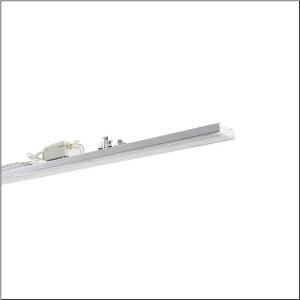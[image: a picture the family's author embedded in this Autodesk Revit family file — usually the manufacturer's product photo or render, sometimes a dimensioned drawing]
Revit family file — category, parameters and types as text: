
# Revit family: licross_11_recessed_mo_51tl18cn49xg
name_source: partatom
category: Lighting Fixtures
units: mm (PartAtom-declared; Revit-internal decimal feet)

## family parameters
Cut with Voids When Loaded = No
Host = Face
Light Source = No
Part Type = Normal
Room Calculation Point = No
Round Connector Dimension = Use Diameter
Shared = No

## types (1)
- --- (1 x LED, 9040 lm, 49.3 W, 4000K)
    Apparent Load = 49 VA
    CIE Flux Codes = 83 96 99 100 100
    Color Rendering = 80
    Color Temperature = 4000K
    Default Elevation = 1800 mm
    Description = Licross 11 Recessed MO, luminaire insert, of sheet steel, coil coated, white, length: 1.500mm, width: 66mm, height: 67mm, LED rated luminous flux: 9.040lm, light colour: 840, SDCM (Standard Deviation of Colour Matching)MacAdam ≤ 2 SDCM (initial), control gear: ON/OFF Multilumen, CLOi, with plug, 3-pole, with phase selection, mains connection: 220..240V, AC, 50/60Hz, start of lifetime: 49W, end of service life: 55W, internal wiring halogen-free, primary light control with lens, of plastic, primary optical cover: cover, of PMMA, light emission: direct distribution, primary light characteristic: symmetric, protection rating (complete): IP40, insulation class (complete): insulation class I (protective earthing), certification: CE, ENEC, VDE, UKCA, protection symbol: D if used in an environment without relevant dust loads with corresponding accessories, impact resistance: IK06, permissible ambient temperature for indoor applications: -35..+40°C, corresponds to IFS (International Featured Standards) requirements for safety and quality in the food industry, reducing of maximum allowable ambient temperature of 5°C with ceiling mounting, LABS conformity tested according to VDMA 24364:2018-05, The light source and the operating device comply with the requirements of the Ecodesign Regulation (EU) 2019/2020 and are replaceable in accordance with this regulation, packaging unit: 1 piece
    Height = 58 mm
    Lamp = 1 x LED
    Lamp Light Flux = 9040 lm
    Lamp Power = 49.3 W
    Lamp count = 1
    Length = 1500 mm
    Luminous efficacy = 183 lm/W
    Manufacturer = Siteco
    ModVariant = No
    Model = 51TL18CN49XG
    Mounting Place = Ceiling
    Mounting Type = Pendant
    Number of Poles = 1
    OnlyDefault = Yes
    Power Factor = 1
    Product Name = Licross 11 Recessed MO
    Product group = luminaire insert | ceiling pendant
    ProductGroupID = 901
    Protection Class = Protection class I
    Protection Degree = IP 40
    RLX_Detail_Level = 1
    RLX_Emergency_Light_Flux = 0 lm
    RLX_Emergency_Type = 0
    RLX_Emergency_Type_DB = No
    RlxData = <blob elided: 22577 chars, md5=b130c7b6>
    Socket = socket
    Standby Power = 0 W
    System Light Flux = 9040 lm
    System Power = 49 W
    Type Comments = factory setting: luminous flux: 100 % | (A | C | E) | 113 mA
    Type Image = l_1296930.jpg
    URL = http://relux.com
    VarID = @adj_000041
    Voltage = 0 V
    Weight = 0.00 kg
    Width = 66 mm

## geometry (parser evidence)
native form markers: Blend x4, Sweep x9
no freeform markers — native parametric forms only
